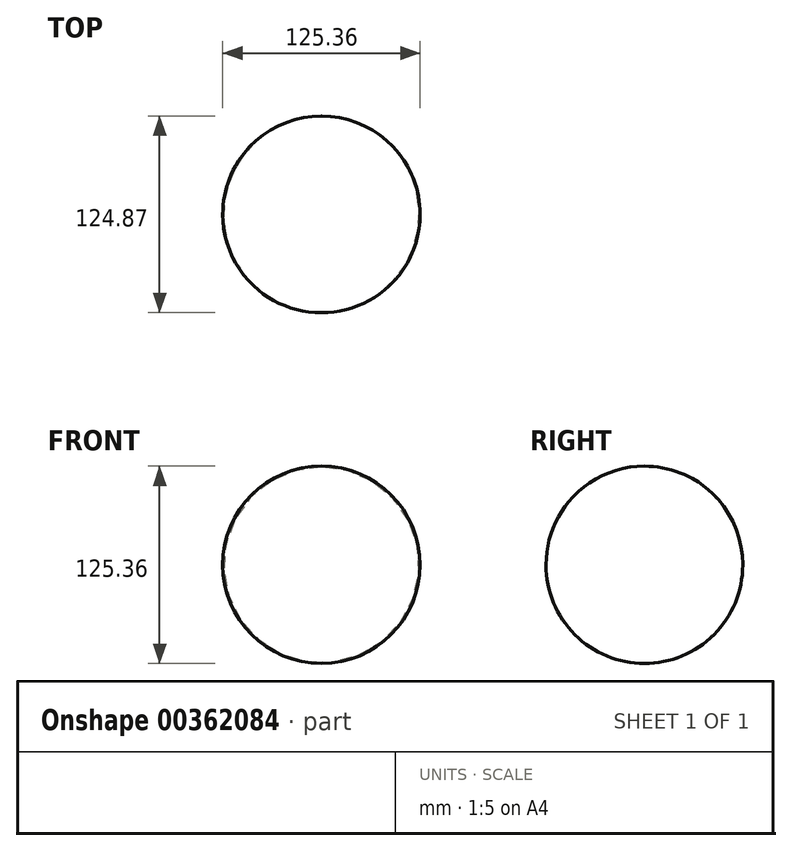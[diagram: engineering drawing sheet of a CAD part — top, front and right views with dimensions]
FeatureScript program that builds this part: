
annotation { "Feature Type Name" : "Feature", "Feature Type Description" : "" }
export const myFeature = defineFeature(function(context is Context, id is Id, definition is map)
    precondition{}
    {
        {
            var Q0;
            Q0=qCreatedBy(makeId("Top.planeOp"),FACE);
            var sketch = newSketch(context, id + "F0", { "sketchPlane" : qUnion([Q0])});
            skPoint(sketch, "E0", {"position": v(0, 0) * mm});
            skArc(sketch, "E1", {"start": v(0, 64.16) * mm, "mid": v(-62.2, 1.73) * mm, "end": v(0, -60.71) * mm});
            skLineSegment(sketch, "E2", {"start": v(0, 64.16) * mm, "end": v(0, -60.71) * mm});
            skSolve(sketch);
        }
        {
            var Q0;
            Q0 = qSketchRegion(id + "F0", true);
            var Q1;
            Q1=sQuery(id+"F0.wireOp",EDGE,"E2");
            revolve(context, id + "F1", {"entities" : qUnion([Q0]), "axis" : qUnion([Q1]), "revolveType" : RevolveType.FULL, "oppositeDirection" : true});
        }
    });
